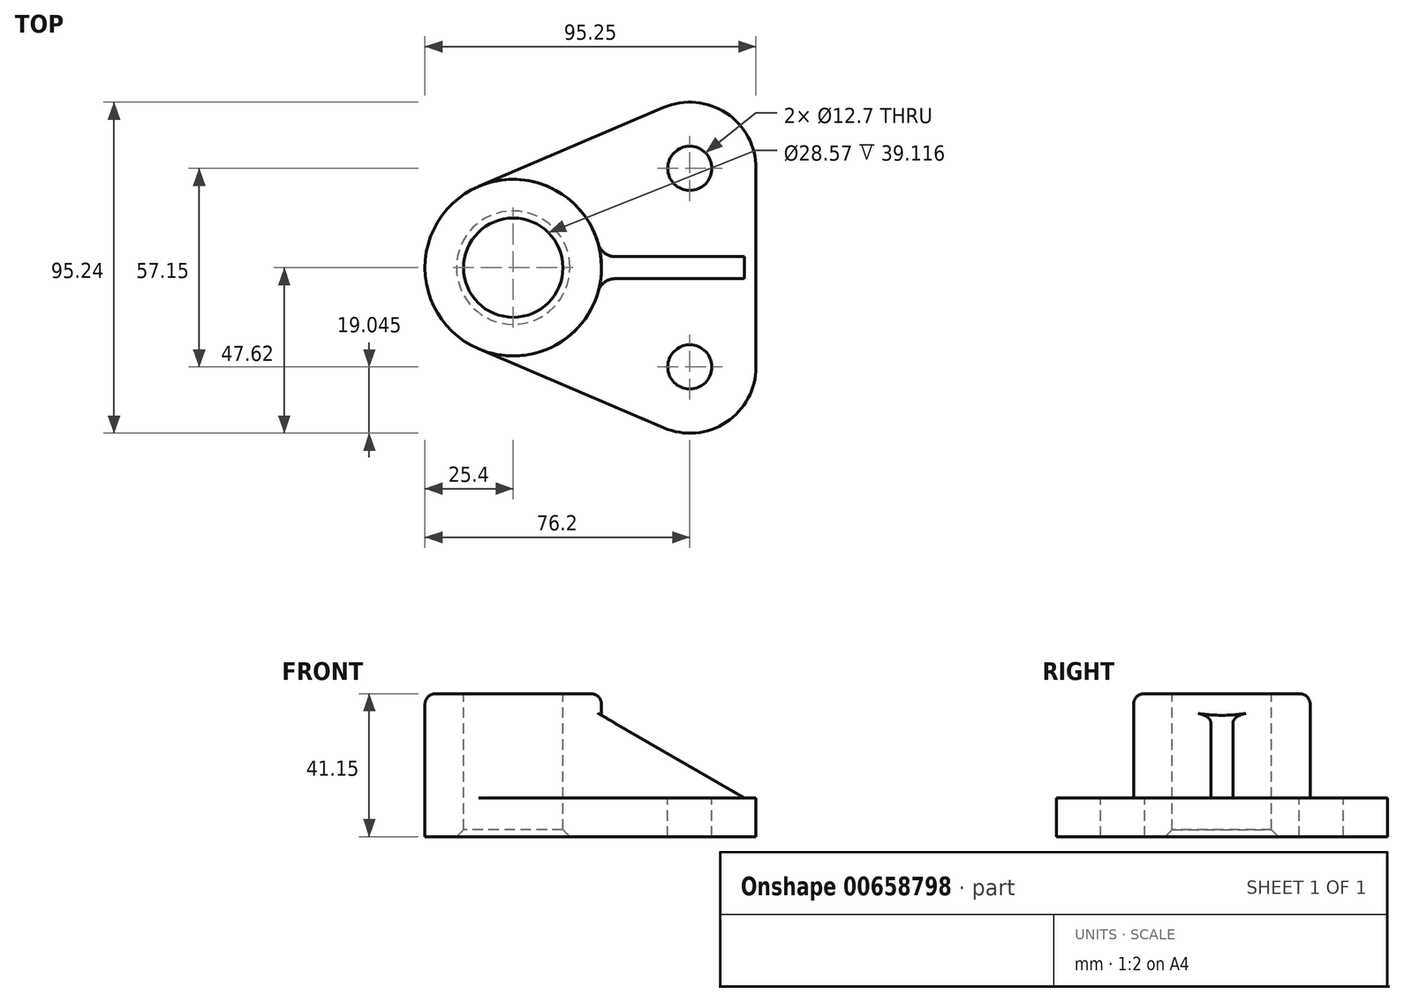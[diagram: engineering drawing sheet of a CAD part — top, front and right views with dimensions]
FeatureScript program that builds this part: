
annotation { "Feature Type Name" : "Feature", "Feature Type Description" : "" }
export const myFeature = defineFeature(function(context is Context, id is Id, definition is map)
    precondition{}
    {
        {
            var Q0;
            Q0=qCreatedBy(makeId("Top.planeOp"),FACE);
            var sketch = newSketch(context, id + "F0", { "sketchPlane" : qUnion([Q0])});
            skCircle(sketch, "E0", {"center": v(0, 0) * mm, "radius": 25.4 * mm});
            skLineSegment(sketch, "E1", {"start": v(0, 0) * mm, "end": v(100.04, 0) * mm, "construction": true});
            skLineSegment(sketch, "E2", {"start": v(-9.97, -23.36) * mm, "end": v(43.33, -46.1) * mm});
            skLineSegment(sketch, "E3", {"start": v(69.85, -28.58) * mm, "end": v(69.85, 28.58) * mm});
            skLineSegment(sketch, "E4", {"start": v(43.33, 46.1) * mm, "end": v(-9.97, 23.36) * mm});
            skPoint(sketch, "E5.visualSharp", {"position": v(69.85, 57.41) * mm});
            skArc(sketch, "E5.filletArc", {"start": v(69.85, 28.58) * mm, "mid": v(61.3, 44.47) * mm, "end": v(43.33, 46.1) * mm});
            skPoint(sketch, "E6.visualSharp", {"position": v(69.85, -57.41) * mm});
            skArc(sketch, "E6.filletArc", {"start": v(43.33, -46.1) * mm, "mid": v(61.3, -44.47) * mm, "end": v(69.85, -28.58) * mm});
            skSolve(sketch);
        }
        {
            var Q0;
            {var subQ1=sQuery(id+"F0.wireOp",EDGE,"E2");Q0=makeQuery(id+"F0.imprint","IMPRINT",FACE,{"disambiguationData":[TD([[makeQuery(id+"F0.imprint","IMPRINT",EDGE,{"derivedFrom":subQ1}),1.0]])]});}
            extrude(context, id + "F1", {"entities" : qUnion([Q0]), "depth" : 11.18 * mm});
        }
        {
            var Q0;
            {var subQ0=sQuery(id+"F0.wireOp",EDGE,"E0");var subQ1=makeQuery(id+"F0.imprint","INTERSECT",VERTEX,{"derivedFrom":[subQ0,sQuery(id+"F0.wireOp",EDGE,"E2")]});Q0=makeQuery(id+"F0.imprint","IMPRINT",FACE,{"disambiguationData":[TD([[makeQuery(id+"F0.imprint","IMPRINT",EDGE,{"disambiguationData":[TD([[subQ1,1.0]])],"derivedFrom":subQ0}),1.0]])]});}
            extrude(context, id + "F2", {"entities" : qUnion([Q0]), "operationType" : NewBodyOperationType.ADD, "depth" : 41.15 * mm});
        }
        {
            var Q0;
            Q0=makeQuery(id+"F2.opExtrude","CAP_FACE",FACE,{"disambiguationData":[OSD([sQuery(id+"F0.wireOp",EDGE,"E0")])],"isStart":false});
            var sketch = newSketch(context, id + "F3", { "sketchPlane" : qUnion([Q0])});
            skCircle(sketch, "E7", {"center": v(0, 0) * mm, "radius": 14.29 * mm});
            skSolve(sketch);
        }
        {
            var Q0;
            Q0=qSketchRegion(id+"F3",true);
            extrude(context, id + "F4", {"entities" : qUnion([Q0]), "operationType" : NewBodyOperationType.REMOVE, "endBound" : BoundingType.THROUGH_ALL, "oppositeDirection" : true, "depth" : 25.4 * mm});
        }
        {
            var Q0;
            Q0=makeQuery(id+"F1.opExtrude","CAP_FACE",FACE,{"disambiguationData":[OSD([sQuery(id+"F0.wireOp",EDGE,"E0"),sQuery(id+"F0.wireOp",EDGE,"E2"),sQuery(id+"F0.wireOp",EDGE,"E3"),sQuery(id+"F0.wireOp",EDGE,"E4"),sQuery(id+"F0.wireOp",EDGE,"E5.filletArc"),sQuery(id+"F0.wireOp",EDGE,"E6.filletArc")])],"isStart":false});
            var sketch = newSketch(context, id + "F5", { "sketchPlane" : qUnion([Q0])});
            skCircle(sketch, "E8", {"center": v(50.8, 28.58) * mm, "radius": 6.35 * mm});
            skCircle(sketch, "E9", {"center": v(50.8, -28.58) * mm, "radius": 6.35 * mm});
            skSolve(sketch);
        }
        {
            var Q0;
            Q0=qSketchRegion(id+"F5",true);
            extrude(context, id + "F6", {"entities" : qUnion([Q0]), "operationType" : NewBodyOperationType.REMOVE, "endBound" : BoundingType.THROUGH_ALL, "oppositeDirection" : true, "depth" : 25.4 * mm});
        }
        {
            var Q0;
            Q0=qCreatedBy(makeId("Front.planeOp"),FACE);
            var sketch = newSketch(context, id + "F7", { "sketchPlane" : qUnion([Q0])});
            skLineSegment(sketch, "E10.0.1", {"start": v(66.55, 11.18) * mm, "end": v(43.33, 11.18) * mm});
            skLineSegment(sketch, "E10.0.2", {"start": v(43.33, 11.18) * mm, "end": v(25.4, 11.18) * mm});
            skLineSegment(sketch, "E10.0.4", {"start": v(25.4, 11.18) * mm, "end": v(43.33, 11.18) * mm});
            skLineSegment(sketch, "E10.0.5", {"start": v(43.33, 11.18) * mm, "end": v(66.55, 11.18) * mm});
            skLineSegment(sketch, "E11", {"start": v(25.42, 34.92) * mm, "end": v(66.55, 11.18) * mm});
            skPoint(sketch, "E10.0.3.end.orphan", {"position": v(25.4, 11.18) * mm});
            skLineSegment(sketch, "E12", {"start": v(25.4, 11.18) * mm, "end": v(22.55, 11.18) * mm});
            skLineSegment(sketch, "E13", {"start": v(22.55, 11.18) * mm, "end": v(22.55, 36.58) * mm});
            skLineSegment(sketch, "E14", {"start": v(22.55, 36.58) * mm, "end": v(25.42, 34.92) * mm});
            skSolve(sketch);
        }
        {
            var Q0;
            Q0=qSketchRegion(id+"F7",true);
            extrude(context, id + "F8", {"entities" : qUnion([Q0]), "operationType" : NewBodyOperationType.ADD, "depth" : 6.35 * mm, "symmetric" : true});
        }
        {
            var Q0;
            Q0=makeQuery(id+"F4.boolean.opBoolean","COPY",EDGE,{"derivedFrom":makeQuery(id+"F4.opExtrude","CAP_EDGE",EDGE,{"disambiguationData":[OSD([sQuery(id+"F3.wireOp",EDGE,"E7")])],"isStart":true})});
            var Q1;
            {var subQ0=sQuery(id+"F0.wireOp",EDGE,"E0");Q1=makeQuery(id+"F4.boolean.opBoolean","INTERSECT",EDGE,{"derivedFrom":[makeQuery(id+"F2.boolean.opBoolean","MERGE",FACE,{"derivedFrom":[makeQuery(id+"F1.opExtrude","CAP_FACE",FACE,{"disambiguationData":[OSD([subQ0,sQuery(id+"F0.wireOp",EDGE,"E2"),sQuery(id+"F0.wireOp",EDGE,"E3"),sQuery(id+"F0.wireOp",EDGE,"E4"),sQuery(id+"F0.wireOp",EDGE,"E5.filletArc"),sQuery(id+"F0.wireOp",EDGE,"E6.filletArc")])],"isStart":true}),makeQuery(id+"F2.opExtrude","CAP_FACE",FACE,{"disambiguationData":[OSD([subQ0])],"isStart":true})]}),makeQuery(id+"F4.opExtrude","SWEPT_FACE",FACE,{"disambiguationData":[OSD([sQuery(id+"F3.wireOp",EDGE,"E7")])]})]});}
            chamfer(context, id + "F9", {"entities" : qUnion([Q0, Q1]), "chamferType" : ChamferType.OFFSET_ANGLE, "width" : 2.03 * mm, "oppositeDirection" : false, "angle" : 45 * degree, "tangentPropagation" : true});
        }
        {
            var Q0;
            Q0=makeQuery(id+"F2.opExtrude","CAP_EDGE",EDGE,{"disambiguationData":[OSD([sQuery(id+"F0.wireOp",EDGE,"E0")])],"isStart":false});
            fillet(context, id + "F10", {"entities" : qUnion([Q0]), "radius" : 3.05 * mm, "tangentPropagation" : true, "allowEdgeOverflow" : false});
        }
        {
            var Q0;
            {var subQ0=sQuery(id+"F0.wireOp",EDGE,"E2");var subQ1=sQuery(id+"F0.wireOp",EDGE,"E0");Q0=makeQuery(id+"F8.boolean.opBoolean","SPLIT",EDGE,{"disambiguationData":[TD([makeQuery(id+"F1.opExtrude","SWEPT_FACE",FACE,{"disambiguationData":[OSD([subQ0])]})])],"derivedFrom":makeQuery(id+"F1.opExtrude","CAP_EDGE",EDGE,{"disambiguationData":[OSD([subQ1])],"isStart":false})});}
            var Q1;
            Q1=makeQuery(id+"F8.boolean.opBoolean","INTERSECT",EDGE,{"derivedFrom":[makeQuery(id+"F2.opExtrude","SWEPT_FACE",FACE,{"disambiguationData":[OSD([sQuery(id+"F0.wireOp",EDGE,"E0")])]}),makeQuery(id+"F8.opExtrude","CAP_FACE",FACE,{"disambiguationData":[OSD([sQuery(id+"F7.wireOp",EDGE,"E10.0.4"),sQuery(id+"F7.wireOp",EDGE,"E10.0.5"),sQuery(id+"F7.wireOp",EDGE,"E11"),sQuery(id+"F7.wireOp",EDGE,"E12"),sQuery(id+"F7.wireOp",EDGE,"E13"),sQuery(id+"F7.wireOp",EDGE,"E14")])],"isStart":false})]});
            var Q2;
            Q2=makeQuery(id+"F8.opExtrude","CAP_EDGE",EDGE,{"disambiguationData":[OSD([sQuery(id+"F7.wireOp",EDGE,"E10.0.4"),sQuery(id+"F7.wireOp",EDGE,"E10.0.5"),sQuery(id+"F7.wireOp",EDGE,"E12")])],"isStart":false});
            var Q3;
            Q3=makeQuery(id+"F8.opExtrude","CAP_EDGE",EDGE,{"disambiguationData":[OSD([sQuery(id+"F7.wireOp",EDGE,"E10.0.4"),sQuery(id+"F7.wireOp",EDGE,"E10.0.5"),sQuery(id+"F7.wireOp",EDGE,"E12")])],"isStart":true});
            var Q4;
            Q4=makeQuery(id+"F8.boolean.opBoolean","INTERSECT",EDGE,{"derivedFrom":[makeQuery(id+"F2.opExtrude","SWEPT_FACE",FACE,{"disambiguationData":[OSD([sQuery(id+"F0.wireOp",EDGE,"E0")])]}),makeQuery(id+"F8.opExtrude","CAP_FACE",FACE,{"disambiguationData":[OSD([sQuery(id+"F7.wireOp",EDGE,"E10.0.4"),sQuery(id+"F7.wireOp",EDGE,"E10.0.5"),sQuery(id+"F7.wireOp",EDGE,"E11"),sQuery(id+"F7.wireOp",EDGE,"E12"),sQuery(id+"F7.wireOp",EDGE,"E13"),sQuery(id+"F7.wireOp",EDGE,"E14")])],"isStart":true})]});
            var Q5;
            {var subQ0=sQuery(id+"F0.wireOp",EDGE,"E4");var subQ1=sQuery(id+"F0.wireOp",EDGE,"E0");Q5=makeQuery(id+"F8.boolean.opBoolean","SPLIT",EDGE,{"disambiguationData":[TD([makeQuery(id+"F1.opExtrude","SWEPT_FACE",FACE,{"disambiguationData":[OSD([subQ0])]})])],"derivedFrom":makeQuery(id+"F1.opExtrude","CAP_EDGE",EDGE,{"disambiguationData":[OSD([subQ1])],"isStart":false})});}
            fillet(context, id + "F11", {"entities" : qUnion([Q0, Q1, Q2, Q3, Q4, Q5]), "radius" : 5.08 * mm, "tangentPropagation" : true, "allowEdgeOverflow" : false});
        }
    });
